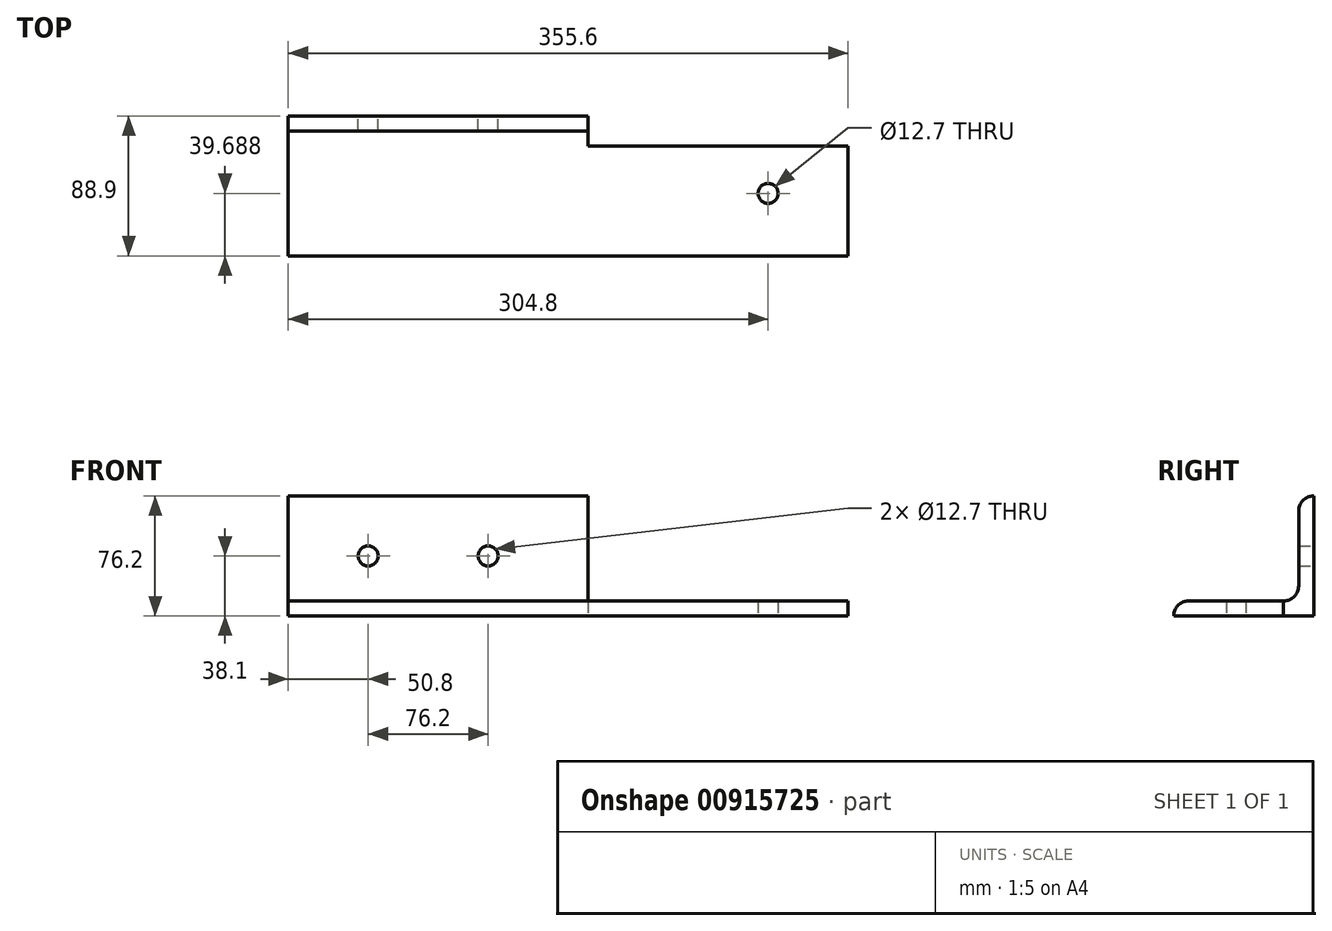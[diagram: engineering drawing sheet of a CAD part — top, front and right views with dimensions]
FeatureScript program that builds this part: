
annotation { "Feature Type Name" : "Feature", "Feature Type Description" : "" }
export const myFeature = defineFeature(function(context is Context, id is Id, definition is map)
    precondition{}
    {
        {
            var Q0;
            Q0=qCreatedBy(makeId("Right.planeOp"),FACE);
            var sketch = newSketch(context, id + "F0", { "sketchPlane" : qUnion([Q0])});
            skLineSegment(sketch, "E0", {"start": v(0, 76.2) * mm, "end": v(0, 0) * mm});
            skLineSegment(sketch, "E1", {"start": v(0, 0) * mm, "end": v(-88.9, 0) * mm});
            skLineSegment(sketch, "E2", {"start": v(-88.9, 0) * mm, "end": v(-88.9, 0) * mm});
            skLineSegment(sketch, "E3", {"start": v(-79.38, 9.53) * mm, "end": v(-19.05, 9.53) * mm});
            skLineSegment(sketch, "E4", {"start": v(-9.52, 19.05) * mm, "end": v(-9.52, 66.67) * mm});
            skLineSegment(sketch, "E5", {"start": v(0, 76.2) * mm, "end": v(0, 76.2) * mm});
            skPoint(sketch, "E6.visualSharp", {"position": v(-9.52, 76.2) * mm});
            skArc(sketch, "E6.filletArc", {"start": v(0, 76.2) * mm, "mid": v(-6.74, 73.41) * mm, "end": v(-9.52, 66.67) * mm});
            skPoint(sketch, "E7.visualSharp", {"position": v(-88.9, 9.52) * mm});
            skArc(sketch, "E7.filletArc", {"start": v(-79.38, 9.53) * mm, "mid": v(-86.11, 6.74) * mm, "end": v(-88.9, 0) * mm});
            skPoint(sketch, "E8.visualSharp", {"position": v(-9.53, 9.53) * mm});
            skArc(sketch, "E8.filletArc", {"start": v(-19.05, 9.53) * mm, "mid": v(-12.31, 12.31) * mm, "end": v(-9.52, 19.05) * mm});
            skSolve(sketch);
        }
        {
            var Q0;
            Q0=qSketchRegion(id+"F0",true);
            extrude(context, id + "F1", {"entities" : qUnion([Q0]), "depth" : 355.6 * mm, "offsetDistance" : 25.4 * mm, "symmetric" : true});
        }
        {
            var Q0;
            Q0=makeQuery(id+"F1.opExtrude","SWEPT_FACE",FACE,{"disambiguationData":[OSD([sQuery(id+"F0.wireOp",EDGE,"E0")])]});
            var sketch = newSketch(context, id + "F2", { "sketchPlane" : qUnion([Q0])});
            skCircle(sketch, "E9", {"center": v(127, 38.1) * mm, "radius": 6.35 * mm});
            skPoint(sketch, "E9.centerSnap0", {"position": v(177.8, 38.1) * mm});
            skCircle(sketch, "E10", {"center": v(50.8, 38.1) * mm, "radius": 6.35 * mm});
            skSolve(sketch);
        }
        {
            var Q0;
            Q0 = qSketchRegion(id + "F2", true);
            extrude(context, id + "F3", {"entities" : qUnion([Q0]), "operationType" : NewBodyOperationType.REMOVE, "oppositeDirection" : true, "depth" : 25.4 * mm, "offsetDistance" : 25.4 * mm});
        }
        {
            var Q0;
            Q0=makeQuery(id+"F1.opExtrude","SWEPT_FACE",FACE,{"disambiguationData":[OSD([sQuery(id+"F0.wireOp",EDGE,"E1")])]});
            var sketch = newSketch(context, id + "F4", { "sketchPlane" : qUnion([Q0])});
            skLineSegment(sketch, "E11.bottom", {"start": v(177.8, 0) * mm, "end": v(12.7, 0) * mm});
            skLineSegment(sketch, "E11.top", {"start": v(177.8, 19.05) * mm, "end": v(12.7, 19.05) * mm});
            skLineSegment(sketch, "E11.left", {"start": v(177.8, 0) * mm, "end": v(177.8, 19.05) * mm});
            skLineSegment(sketch, "E11.right", {"start": v(12.7, 0) * mm, "end": v(12.7, 19.05) * mm});
            skSolve(sketch);
        }
        {
            var Q0;
            Q0 = qSketchRegion(id + "F4", true);
            extrude(context, id + "F5", {"entities" : qUnion([Q0]), "operationType" : NewBodyOperationType.REMOVE, "endBound" : BoundingType.THROUGH_ALL, "oppositeDirection" : true, "depth" : 25.4 * mm, "offsetDistance" : 25.4 * mm});
        }
        {
            var Q0;
            Q0=makeQuery(id+"F1.opExtrude","SWEPT_FACE",FACE,{"disambiguationData":[OSD([sQuery(id+"F0.wireOp",EDGE,"E1")])]});
            var sketch = newSketch(context, id + "F6", { "sketchPlane" : qUnion([Q0])});
            skCircle(sketch, "E12", {"center": v(127, 49.21) * mm, "radius": 6.35 * mm});
            skPoint(sketch, "E12.centerSnap0", {"position": v(177.8, 53.97) * mm});
            skLineSegment(sketch, "E13", {"start": v(12.7, 19.05) * mm, "end": v(12.7, 9.52) * mm});
            skSolve(sketch);
        }
        {
            var Q0;
            Q0 = qSketchRegion(id + "F6", true);
            extrude(context, id + "F7", {"entities" : qUnion([Q0]), "operationType" : NewBodyOperationType.REMOVE, "oppositeDirection" : true, "depth" : 25.4 * mm, "offsetDistance" : 25.4 * mm});
        }
    });
